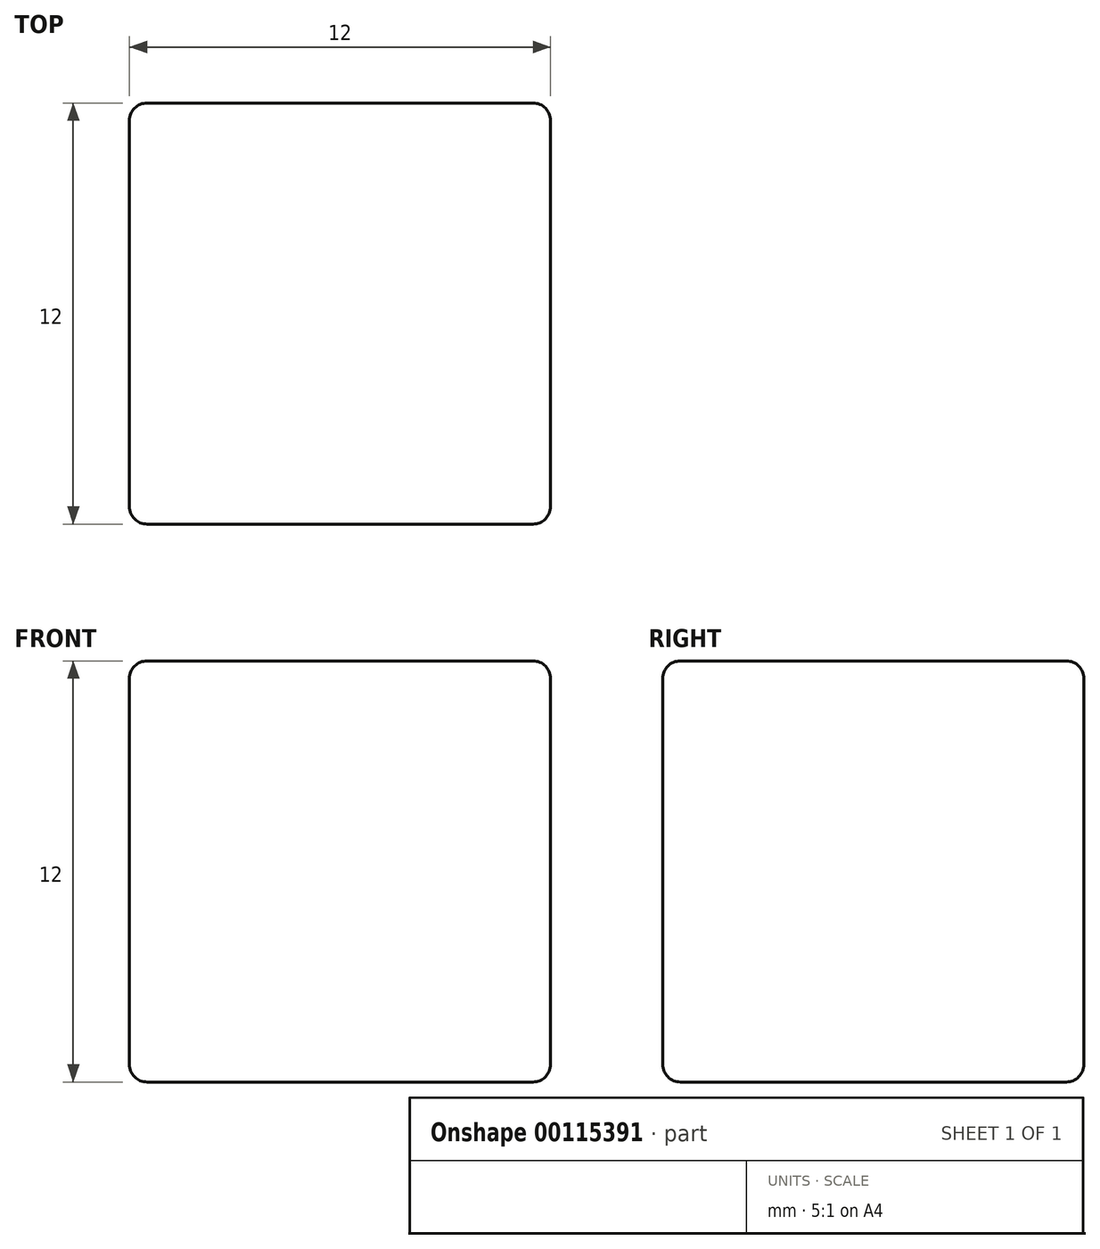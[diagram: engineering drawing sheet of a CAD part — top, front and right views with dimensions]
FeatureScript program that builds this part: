
annotation { "Feature Type Name" : "Feature", "Feature Type Description" : "" }
export const myFeature = defineFeature(function(context is Context, id is Id, definition is map)
    precondition{}
    {
        {
            var Q0;
            Q0=qCreatedBy(makeId("Front.planeOp"),FACE);
            var sketch = newSketch(context, id + "F0", { "sketchPlane" : qUnion([Q0])});
            skLineSegment(sketch, "E0.bottom", {"start": v(-6, 6) * mm, "end": v(6, 6) * mm});
            skLineSegment(sketch, "E0.top", {"start": v(-6, -6) * mm, "end": v(6, -6) * mm});
            skLineSegment(sketch, "E0.left", {"start": v(-6, 6) * mm, "end": v(-6, -6) * mm});
            skLineSegment(sketch, "E0.right", {"start": v(6, 6) * mm, "end": v(6, -6) * mm});
            skPoint(sketch, "E0.middle", {"position": v(0, 0) * mm});
            skSolve(sketch);
        }
        {
            var Q0;
            Q0=makeQuery(id+"F0.imprint","IMPRINT",FACE,{"disambiguationData":[TD([[makeQuery(id+"F0.imprint","IMPRINT",EDGE,{"derivedFrom":sQuery(id+"F0.wireOp",EDGE,"E0.bottom")}),-1.0]])]});
            extrude(context, id + "F1", {"entities" : qUnion([Q0]), "endBound" : BoundingType.SYMMETRIC, "depth" : 12 * mm});
        }
        {
            var Q0;
            Q0=makeQuery(id+"F1.opExtrude","CAP_FACE",FACE,{"disambiguationData":[OSD([sQuery(id+"F0.wireOp",EDGE,"E0.bottom"),sQuery(id+"F0.wireOp",EDGE,"E0.top"),sQuery(id+"F0.wireOp",EDGE,"E0.left"),sQuery(id+"F0.wireOp",EDGE,"E0.right")])],"isStart":false});
            var Q1;
            Q1=makeQuery(id+"F1.opExtrude","SWEPT_FACE",FACE,{"disambiguationData":[OSD([sQuery(id+"F0.wireOp",EDGE,"E0.right")])]});
            var Q2;
            Q2=makeQuery(id+"F1.opExtrude","SWEPT_FACE",FACE,{"disambiguationData":[OSD([sQuery(id+"F0.wireOp",EDGE,"E0.bottom")])]});
            var Q3;
            Q3=makeQuery(id+"F1.opExtrude","SWEPT_FACE",FACE,{"disambiguationData":[OSD([sQuery(id+"F0.wireOp",EDGE,"E0.left")])]});
            var Q4;
            Q4=makeQuery(id+"F1.opExtrude","SWEPT_FACE",FACE,{"disambiguationData":[OSD([sQuery(id+"F0.wireOp",EDGE,"E0.top")])]});
            var Q5;
            Q5=makeQuery(id+"F1.opExtrude","CAP_FACE",FACE,{"disambiguationData":[OSD([sQuery(id+"F0.wireOp",EDGE,"E0.bottom"),sQuery(id+"F0.wireOp",EDGE,"E0.top"),sQuery(id+"F0.wireOp",EDGE,"E0.left"),sQuery(id+"F0.wireOp",EDGE,"E0.right")])],"isStart":true});
            fillet(context, id + "F2", {"entities" : qUnion([Q0, Q1, Q2, Q3, Q4, Q5]), "radius" : .5 * mm, "tangentPropagation" : true, "allowEdgeOverflow" : false});
        }
    });
